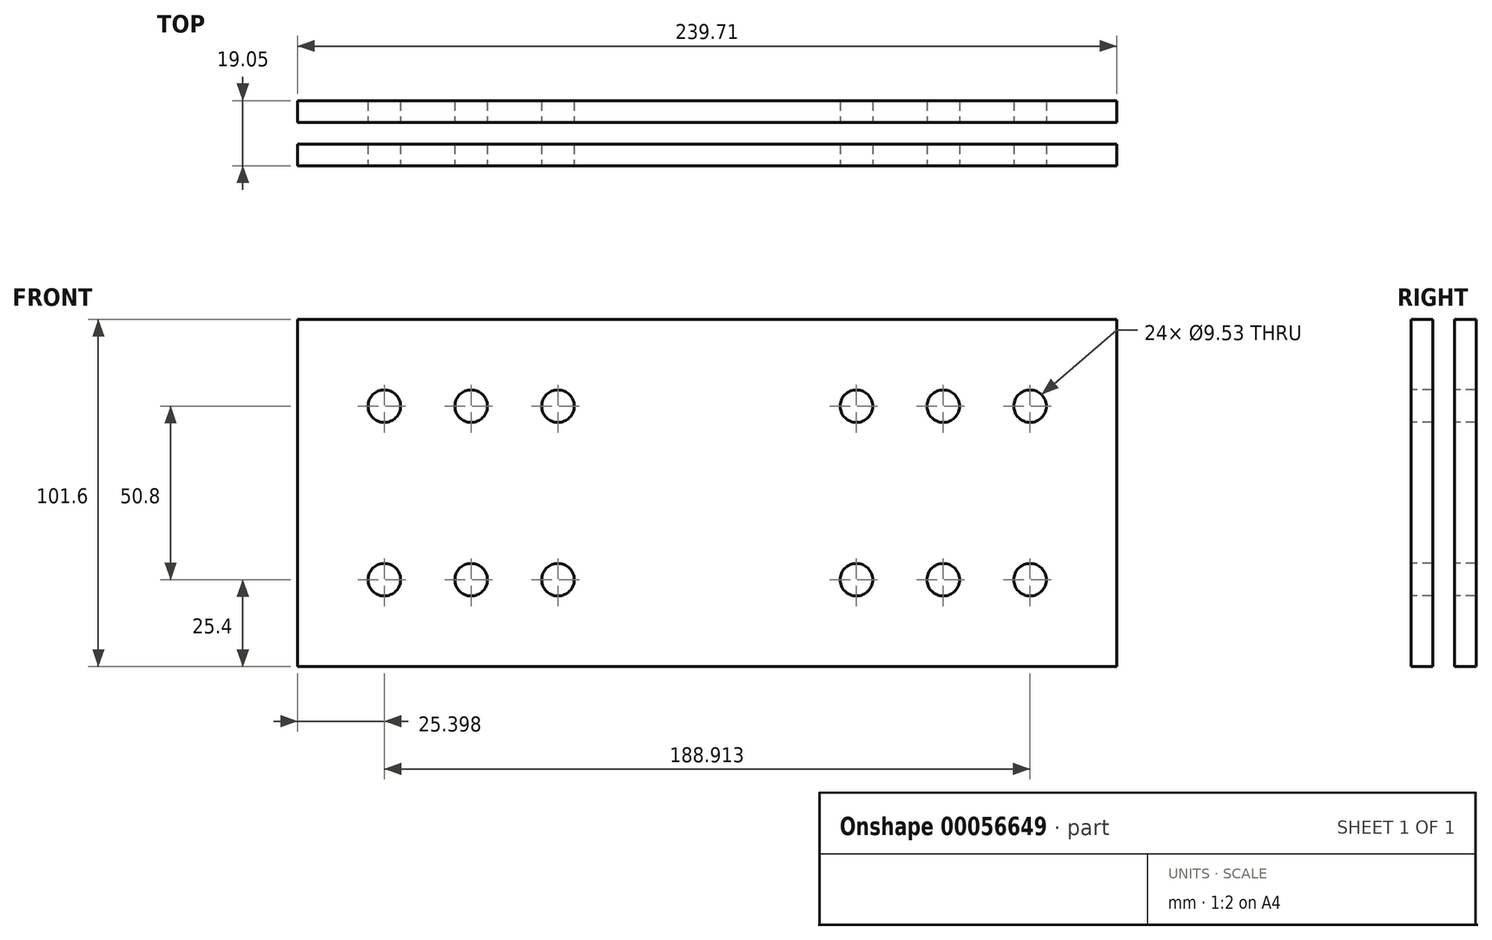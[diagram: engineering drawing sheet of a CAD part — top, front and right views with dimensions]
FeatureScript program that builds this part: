
annotation { "Feature Type Name" : "Feature", "Feature Type Description" : "" }
export const myFeature = defineFeature(function(context is Context, id is Id, definition is map)
    precondition{}
    {
        {
            var Q0;
            Q0=qCreatedBy(makeId("Top.planeOp"),FACE);
            var sketch = newSketch(context, id + "F0", { "sketchPlane" : qUnion([Q0])});
            skLineSegment(sketch, "E0.bottom", {"start": v(-111.75, 41.24) * mm, "end": v(127.96, 41.24) * mm});
            skLineSegment(sketch, "E0.top", {"start": v(-111.75, 34.89) * mm, "end": v(127.96, 34.89) * mm});
            skLineSegment(sketch, "E0.left", {"start": v(-111.75, 41.24) * mm, "end": v(-111.75, 34.89) * mm});
            skLineSegment(sketch, "E0.right", {"start": v(127.96, 41.24) * mm, "end": v(127.96, 34.89) * mm});
            skLineSegment(sketch, "E1.0.1.0", {"start": v(-111.75, 22.19) * mm, "end": v(127.96, 22.19) * mm});
            skLineSegment(sketch, "E1.0.1.1", {"start": v(-111.75, 28.54) * mm, "end": v(-111.75, 22.19) * mm});
            skLineSegment(sketch, "E1.0.1.2", {"start": v(127.96, 28.54) * mm, "end": v(127.96, 22.19) * mm});
            skLineSegment(sketch, "E1.0.1.3", {"start": v(-111.75, 28.54) * mm, "end": v(127.96, 28.54) * mm});
            skLineSegment(sketch, "E1.direction1", {"start": v(-111.75, 34.89) * mm, "end": v(-56.2, 34.89) * mm, "construction": true});
            skLineSegment(sketch, "E1.direction2", {"start": v(-111.75, 34.89) * mm, "end": v(-111.75, 22.19) * mm, "construction": true});
            skSolve(sketch);
        }
        {
            var Q0;
            Q0 = qSketchRegion(id + "F0", true);
            extrude(context, id + "F1", {"entities" : qUnion([Q0]), "endBound" : BoundingType.SYMMETRIC, "depth" : 101.6 * mm});
        }
        {
            var Q0;
            Q0=makeQuery(id+"F1.opExtrude","SWEPT_FACE",FACE,{"disambiguationData":[OSD([sQuery(id+"F0.wireOp",EDGE,"E1.0.1.0")])]});
            var sketch = newSketch(context, id + "F2", { "sketchPlane" : qUnion([Q0])});
            skCircle(sketch, "E2", {"center": v(-86.35, 25.4) * mm, "radius": 4.76 * mm});
            skCircle(sketch, "E3", {"center": v(102.56, 25.4) * mm, "radius": 4.76 * mm});
            skCircle(sketch, "E4.0.1.0", {"center": v(-86.35, -25.4) * mm, "radius": 4.76 * mm});
            skCircle(sketch, "E4.1.0.0", {"center": v(-60.95, 25.4) * mm, "radius": 4.76 * mm});
            skCircle(sketch, "E4.1.1.0", {"center": v(-60.95, -25.4) * mm, "radius": 4.76 * mm});
            skCircle(sketch, "E4.2.0.0", {"center": v(-35.55, 25.4) * mm, "radius": 4.76 * mm});
            skCircle(sketch, "E4.2.1.0", {"center": v(-35.55, -25.4) * mm, "radius": 4.76 * mm});
            skLineSegment(sketch, "E4.direction1", {"start": v(-86.35, 25.4) * mm, "end": v(-60.95, 25.4) * mm, "construction": true});
            skLineSegment(sketch, "E4.direction2", {"start": v(-86.35, 25.4) * mm, "end": v(-86.35, -25.4) * mm, "construction": true});
            skCircle(sketch, "E5.0.1.0", {"center": v(102.56, -25.4) * mm, "radius": 4.76 * mm});
            skCircle(sketch, "E5.1.0.0", {"center": v(77.16, 25.4) * mm, "radius": 4.76 * mm});
            skCircle(sketch, "E5.1.1.0", {"center": v(77.16, -25.4) * mm, "radius": 4.76 * mm});
            skCircle(sketch, "E5.2.0.0", {"center": v(51.76, 25.4) * mm, "radius": 4.76 * mm});
            skCircle(sketch, "E5.2.1.0", {"center": v(51.76, -25.4) * mm, "radius": 4.76 * mm});
            skLineSegment(sketch, "E5.direction1", {"start": v(102.56, 25.4) * mm, "end": v(77.16, 25.4) * mm, "construction": true});
            skLineSegment(sketch, "E5.direction2", {"start": v(102.56, 25.4) * mm, "end": v(102.56, -25.4) * mm, "construction": true});
            skSolve(sketch);
        }
        {
            var Q0;
            Q0 = qSketchRegion(id + "F2", true);
            extrude(context, id + "F3", {"entities" : qUnion([Q0]), "operationType" : NewBodyOperationType.REMOVE, "endBound" : BoundingType.THROUGH_ALL, "oppositeDirection" : true, "depth" : 25.4 * mm});
        }
    });
